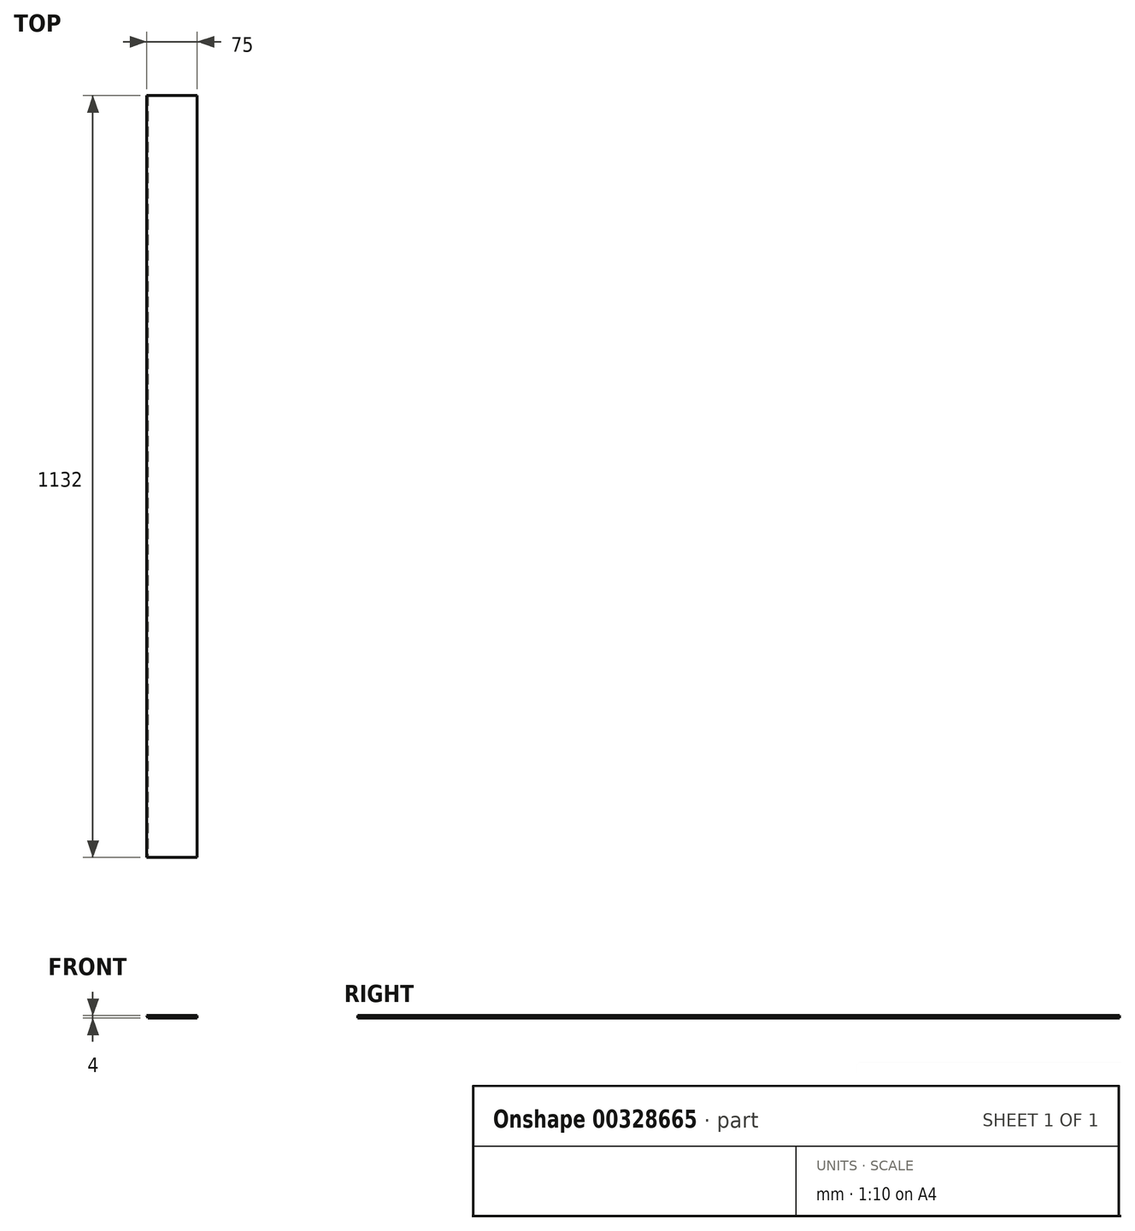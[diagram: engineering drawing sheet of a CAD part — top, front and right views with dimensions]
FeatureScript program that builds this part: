
annotation { "Feature Type Name" : "Feature", "Feature Type Description" : "" }
export const myFeature = defineFeature(function(context is Context, id is Id, definition is map)
    precondition{}
    {
        {
            var Q0;
            Q0=qCreatedBy(makeId("Front.planeOp"),FACE);
            var sketch = newSketch(context, id + "F0", { "sketchPlane" : qUnion([Q0])});
            skLineSegment(sketch, "E0", {"start": v(0, 0) * mm, "end": v(75, 0) * mm});
            skLineSegment(sketch, "E1", {"start": v(75, 0) * mm, "end": v(75, -4) * mm});
            skLineSegment(sketch, "E2", {"start": v(75, -4) * mm, "end": v(1.66, -4) * mm});
            skLineSegment(sketch, "E3", {"start": v(1.66, -4) * mm, "end": v(0, 0) * mm});
            skSolve(sketch);
        }
        {
            var Q0;
            Q0=qSketchRegion(id+"F0",true);
            extrude(context, id + "F1", {"entities" : qUnion([Q0]), "oppositeDirection" : true, "depth" : 1132 * mm});
        }
    });
